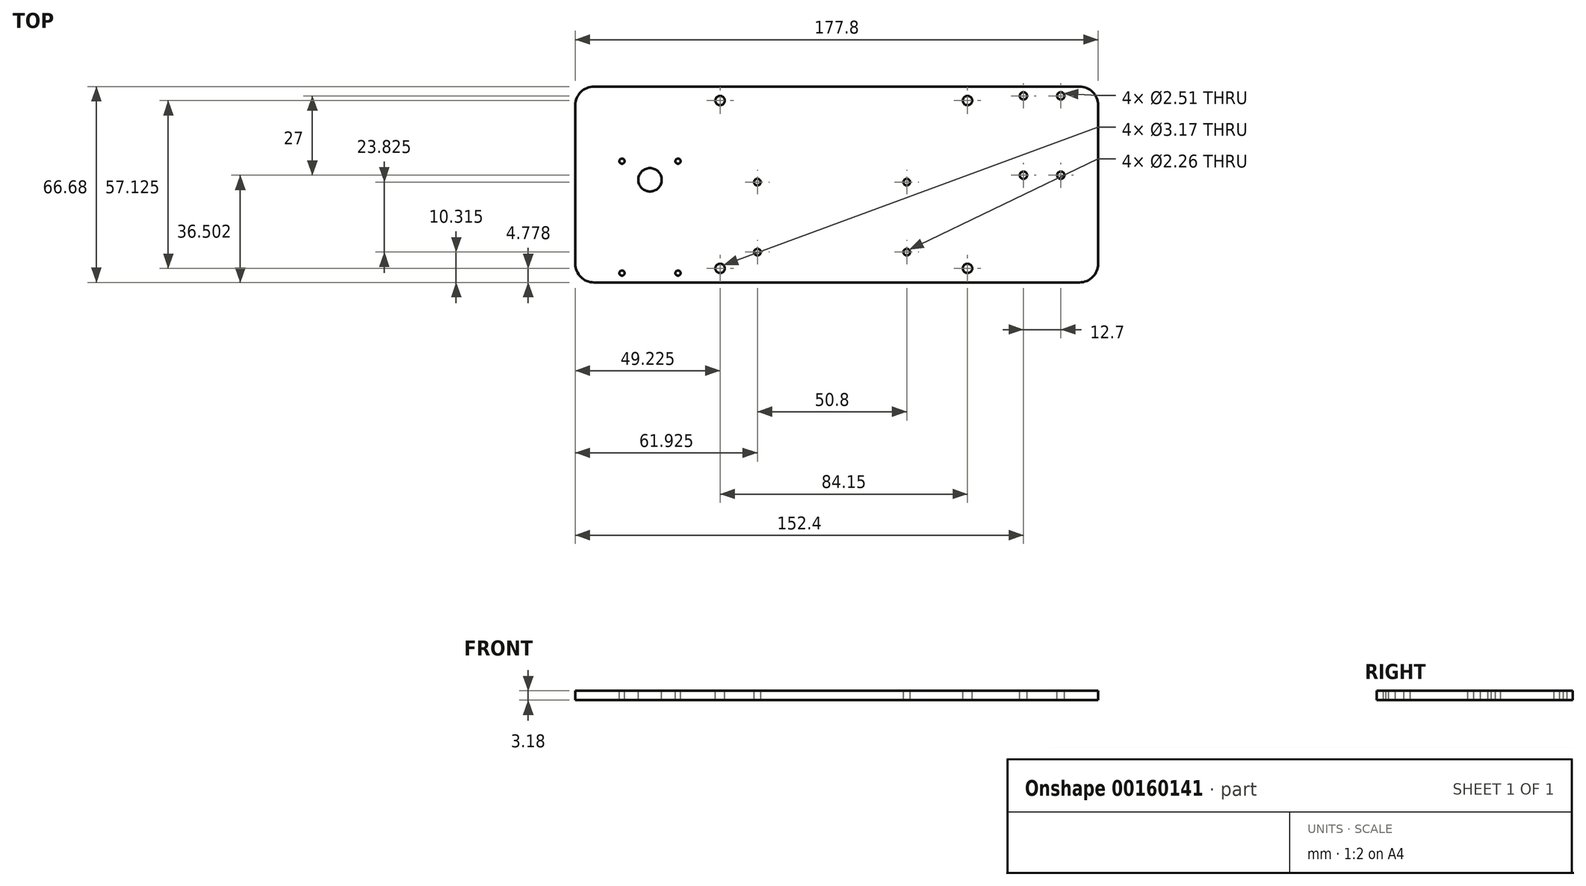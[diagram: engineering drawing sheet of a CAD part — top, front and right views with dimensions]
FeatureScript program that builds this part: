
annotation { "Feature Type Name" : "Feature", "Feature Type Description" : "" }
export const myFeature = defineFeature(function(context is Context, id is Id, definition is map)
    precondition{}
    {
        {
            var Q0;
            Q0=qCreatedBy(makeId("Top.planeOp"),FACE);
            var sketch = newSketch(context, id + "F0", { "sketchPlane" : qUnion([Q0])});
            skLineSegment(sketch, "E0.bottom", {"start": v(88.9, -33.34) * mm, "end": v(-88.9, -33.34) * mm});
            skLineSegment(sketch, "E0.top", {"start": v(88.9, 33.34) * mm, "end": v(-88.9, 33.34) * mm});
            skLineSegment(sketch, "E0.left", {"start": v(88.9, -33.34) * mm, "end": v(88.9, 33.34) * mm});
            skLineSegment(sketch, "E0.right", {"start": v(-88.9, -33.34) * mm, "end": v(-88.9, 33.34) * mm});
            skPoint(sketch, "E0.middle", {"position": v(0, 0) * mm});
            skSolve(sketch);
        }
        {
            var Q0;
            Q0 = qSketchRegion(id + "F0", true);
            extrude(context, id + "F1", {"entities" : qUnion([Q0]), "depth" : 3.17 * mm});
        }
        {
            var Q0;
            Q0=makeQuery(id+"F1.opExtrude","CAP_FACE",FACE,{"disambiguationData":[OSD([sQuery(id+"F0.wireOp",EDGE,"E0.bottom"),sQuery(id+"F0.wireOp",EDGE,"E0.top"),sQuery(id+"F0.wireOp",EDGE,"E0.left"),sQuery(id+"F0.wireOp",EDGE,"E0.right")])],"isStart":false});
            var sketch = newSketch(context, id + "F2", { "sketchPlane" : qUnion([Q0])});
            skLineSegment(sketch, "E1", {"start": v(-104.96, 26.99) * mm, "end": v(-63.7, 26.99) * mm, "construction": true});
            skLineSegment(sketch, "E2", {"start": v(-82.55, 35.77) * mm, "end": v(-82.55, 22.57) * mm, "construction": true});
            skArc(sketch, "E3", {"start": v(-82.55, 33.34) * mm, "mid": v(-87.04, 31.48) * mm, "end": v(-88.9, 26.99) * mm});
            skSolve(sketch);
        }
        {
            var Q0;
            Q0 = qSketchRegion(id + "F2", true);
            var Q1;
            {var subQ0=sQuery(id+"F2.wireOp",EDGE,"E3");Q1=makeQuery(id+"F2.imprint","IMPRINT",FACE,{"disambiguationData":[TD([[makeQuery(id+"F2.imprint","IMPRINT",EDGE,{"derivedFrom":subQ0}),-1.0]])]});}
            extrude(context, id + "F3", {"entities" : qUnion([Q0, Q1]), "operationType" : NewBodyOperationType.REMOVE, "endBound" : BoundingType.THROUGH_ALL, "oppositeDirection" : true, "depth" : 25.4 * mm});
        }
        {
            var Q0;
            Q0=makeQuery(id+"F1.opExtrude","CAP_FACE",FACE,{"disambiguationData":[OSD([sQuery(id+"F0.wireOp",EDGE,"E0.bottom"),sQuery(id+"F0.wireOp",EDGE,"E0.top"),sQuery(id+"F0.wireOp",EDGE,"E0.left"),sQuery(id+"F0.wireOp",EDGE,"E0.right")])],"isStart":false});
            var sketch = newSketch(context, id + "F4", { "sketchPlane" : qUnion([Q0])});
            skLineSegment(sketch, "E4", {"start": v(-93.93, -26.99) * mm, "end": v(97.13, -26.99) * mm, "construction": true});
            skLineSegment(sketch, "E5", {"start": v(-82.55, 36) * mm, "end": v(-82.55, -44.72) * mm, "construction": true});
            skLineSegment(sketch, "E6", {"start": v(82.55, 36.74) * mm, "end": v(82.55, -46.7) * mm, "construction": true});
            skLineSegment(sketch, "E7", {"start": v(-88.9, 26.99) * mm, "end": v(88.9, 26.99) * mm, "construction": true});
            skArc(sketch, "E8", {"start": v(-88.9, -26.99) * mm, "mid": v(-87.04, -31.48) * mm, "end": v(-82.55, -33.34) * mm});
            skArc(sketch, "E9", {"start": v(88.9, 26.99) * mm, "mid": v(87.04, 31.48) * mm, "end": v(82.55, 33.34) * mm});
            skArc(sketch, "E10", {"start": v(82.55, -33.34) * mm, "mid": v(87.04, -31.48) * mm, "end": v(88.9, -26.99) * mm});
            skSolve(sketch);
        }
        {
            var Q0;
            {var subQ0=sQuery(id+"F4.wireOp",EDGE,"E9");Q0=makeQuery(id+"F4.imprint","IMPRINT",FACE,{"disambiguationData":[TD([[makeQuery(id+"F4.imprint","IMPRINT",EDGE,{"derivedFrom":subQ0}),-1.0]])]});}
            var Q1;
            {var subQ0=sQuery(id+"F4.wireOp",EDGE,"E10");Q1=makeQuery(id+"F4.imprint","IMPRINT",FACE,{"disambiguationData":[TD([[makeQuery(id+"F4.imprint","IMPRINT",EDGE,{"derivedFrom":subQ0}),-1.0]])]});}
            var Q2;
            {var subQ0=sQuery(id+"F4.wireOp",EDGE,"E8");Q2=makeQuery(id+"F4.imprint","IMPRINT",FACE,{"disambiguationData":[TD([[makeQuery(id+"F4.imprint","IMPRINT",EDGE,{"derivedFrom":subQ0}),-1.0]])]});}
            extrude(context, id + "F5", {"entities" : qUnion([Q0, Q1, Q2]), "operationType" : NewBodyOperationType.REMOVE, "endBound" : BoundingType.THROUGH_ALL, "oppositeDirection" : true, "depth" : 25.4 * mm});
        }
        {
            var Q0;
            Q0=makeQuery(id+"F1.opExtrude","CAP_FACE",FACE,{"disambiguationData":[OSD([sQuery(id+"F0.wireOp",EDGE,"E0.bottom"),sQuery(id+"F0.wireOp",EDGE,"E0.top"),sQuery(id+"F0.wireOp",EDGE,"E0.left"),sQuery(id+"F0.wireOp",EDGE,"E0.right")])],"isStart":false});
            var sketch = newSketch(context, id + "F6", { "sketchPlane" : qUnion([Q0])});
            skLineSegment(sketch, "E11", {"start": v(-75.5, 30.16) * mm, "end": v(76.36, 30.16) * mm, "construction": true});
            skLineSegment(sketch, "E12", {"start": v(76.2, 36.57) * mm, "end": v(76.2, 3.16) * mm, "construction": true});
            skLineSegment(sketch, "E13", {"start": v(63.5, 36.77) * mm, "end": v(63.5, 3.16) * mm, "construction": true});
            skLineSegment(sketch, "E14", {"start": v(54.23, 3.16) * mm, "end": v(81, 3.16) * mm, "construction": true});
            skCircle(sketch, "E15", {"center": v(63.5, 30.16) * mm, "radius": 1.26 * mm});
            skCircle(sketch, "E16", {"center": v(76.2, 30.16) * mm, "radius": 1.26 * mm});
            skCircle(sketch, "E17", {"center": v(63.5, 3.16) * mm, "radius": 1.26 * mm});
            skCircle(sketch, "E18", {"center": v(76.2, 3.16) * mm, "radius": 1.26 * mm});
            skSolve(sketch);
        }
        {
            var Q0;
            Q0 = qSketchRegion(id + "F6", true);
            extrude(context, id + "F7", {"entities" : qUnion([Q0]), "operationType" : NewBodyOperationType.REMOVE, "endBound" : BoundingType.THROUGH_ALL, "oppositeDirection" : true, "depth" : 25.4 * mm});
        }
        {
            var Q0;
            Q0=makeQuery(id+"F1.opExtrude","CAP_FACE",FACE,{"disambiguationData":[OSD([sQuery(id+"F0.wireOp",EDGE,"E0.bottom"),sQuery(id+"F0.wireOp",EDGE,"E0.top"),sQuery(id+"F0.wireOp",EDGE,"E0.left"),sQuery(id+"F0.wireOp",EDGE,"E0.right")])],"isStart":false});
            var sketch = newSketch(context, id + "F8", { "sketchPlane" : qUnion([Q0])});
            skLineSegment(sketch, "E19", {"start": v(44.48, 28.56) * mm, "end": v(44.48, -28.56) * mm, "construction": true});
            skLineSegment(sketch, "E20", {"start": v(-39.67, 28.56) * mm, "end": v(-39.67, -28.56) * mm, "construction": true});
            skLineSegment(sketch, "E21", {"start": v(-39.67, -28.56) * mm, "end": v(44.48, -28.56) * mm, "construction": true});
            skLineSegment(sketch, "E22", {"start": v(-39.67, 28.56) * mm, "end": v(44.48, 28.56) * mm, "construction": true});
            skCircle(sketch, "E23", {"center": v(44.48, 28.56) * mm, "radius": 1.59 * mm});
            skCircle(sketch, "E24", {"center": v(-39.67, 28.56) * mm, "radius": 1.59 * mm});
            skCircle(sketch, "E25", {"center": v(-39.67, -28.56) * mm, "radius": 1.59 * mm});
            skCircle(sketch, "E26", {"center": v(44.48, -28.56) * mm, "radius": 1.59 * mm});
            skSolve(sketch);
        }
        {
            var Q0;
            Q0 = qSketchRegion(id + "F8", true);
            extrude(context, id + "F9", {"entities" : qUnion([Q0]), "operationType" : NewBodyOperationType.REMOVE, "endBound" : BoundingType.THROUGH_ALL, "oppositeDirection" : true, "depth" : 25.4 * mm});
        }
        {
            var Q0;
            Q0=makeQuery(id+"F1.opExtrude","CAP_FACE",FACE,{"disambiguationData":[OSD([sQuery(id+"F0.wireOp",EDGE,"E0.bottom"),sQuery(id+"F0.wireOp",EDGE,"E0.top"),sQuery(id+"F0.wireOp",EDGE,"E0.left"),sQuery(id+"F0.wireOp",EDGE,"E0.right")])],"isStart":false});
            var sketch = newSketch(context, id + "F10", { "sketchPlane" : qUnion([Q0])});
            skLineSegment(sketch, "E27", {"start": v(-76.57, 7.94) * mm, "end": v(-41.84, 7.94) * mm, "construction": true});
            skLineSegment(sketch, "E28", {"start": v(-74.45, -30.16) * mm, "end": v(-51.24, -30.16) * mm, "construction": true});
            skLineSegment(sketch, "E29", {"start": v(-73.03, 19.17) * mm, "end": v(-73.03, -53.87) * mm, "construction": true});
            skLineSegment(sketch, "E30", {"start": v(-53.98, 17.58) * mm, "end": v(-53.98, -54.33) * mm, "construction": true});
            skCircle(sketch, "E31", {"center": v(-73.03, 7.94) * mm, "radius": 0.89 * mm});
            skCircle(sketch, "E32", {"center": v(-53.98, 7.94) * mm, "radius": 0.89 * mm});
            skCircle(sketch, "E33", {"center": v(-73.03, -30.16) * mm, "radius": 0.89 * mm});
            skCircle(sketch, "E34", {"center": v(-53.98, -30.16) * mm, "radius": 0.89 * mm});
            skSolve(sketch);
        }
        {
            var Q0;
            Q0 = qSketchRegion(id + "F10", true);
            extrude(context, id + "F11", {"entities" : qUnion([Q0]), "operationType" : NewBodyOperationType.REMOVE, "endBound" : BoundingType.THROUGH_ALL, "oppositeDirection" : true, "depth" : 25.4 * mm});
        }
        {
            var Q0;
            Q0=makeQuery(id+"F1.opExtrude","CAP_FACE",FACE,{"disambiguationData":[OSD([sQuery(id+"F0.wireOp",EDGE,"E0.bottom"),sQuery(id+"F0.wireOp",EDGE,"E0.top"),sQuery(id+"F0.wireOp",EDGE,"E0.left"),sQuery(id+"F0.wireOp",EDGE,"E0.right")])],"isStart":false});
            var sketch = newSketch(context, id + "F12", { "sketchPlane" : qUnion([Q0])});
            skLineSegment(sketch, "E35", {"start": v(-99.2, 1.59) * mm, "end": v(-41.85, 1.59) * mm, "construction": true});
            skLineSegment(sketch, "E36", {"start": v(-63.5, 16.63) * mm, "end": v(-63.5, -36.81) * mm, "construction": true});
            skCircle(sketch, "E37", {"center": v(-63.5, 1.59) * mm, "radius": 3.98 * mm});
            skSolve(sketch);
        }
        {
            var Q0;
            Q0 = qSketchRegion(id + "F12", true);
            extrude(context, id + "F13", {"entities" : qUnion([Q0]), "operationType" : NewBodyOperationType.REMOVE, "endBound" : BoundingType.THROUGH_ALL, "oppositeDirection" : true, "depth" : 25.4 * mm});
        }
        {
            var Q0;
            Q0=makeQuery(id+"F1.opExtrude","CAP_FACE",FACE,{"disambiguationData":[OSD([sQuery(id+"F0.wireOp",EDGE,"E0.bottom"),sQuery(id+"F0.wireOp",EDGE,"E0.top"),sQuery(id+"F0.wireOp",EDGE,"E0.left"),sQuery(id+"F0.wireOp",EDGE,"E0.right")])],"isStart":false});
            var sketch = newSketch(context, id + "F14", { "sketchPlane" : qUnion([Q0])});
            skLineSegment(sketch, "E38", {"start": v(-33.95, -23.03) * mm, "end": v(44.85, -23.03) * mm, "construction": true});
            skLineSegment(sketch, "E39", {"start": v(-28.14, 0.8) * mm, "end": v(34.53, 0.8) * mm, "construction": true});
            skLineSegment(sketch, "E40", {"start": v(-26.97, 8) * mm, "end": v(-26.97, -25.96) * mm, "construction": true});
            skLineSegment(sketch, "E41", {"start": v(23.83, 9.29) * mm, "end": v(23.83, -25.96) * mm, "construction": true});
            skCircle(sketch, "E42", {"center": v(-26.97, 0.8) * mm, "radius": 1.13 * mm});
            skCircle(sketch, "E43", {"center": v(23.83, 0.8) * mm, "radius": 1.13 * mm});
            skCircle(sketch, "E44", {"center": v(23.83, -23.03) * mm, "radius": 1.13 * mm});
            skCircle(sketch, "E45", {"center": v(-26.97, -23.03) * mm, "radius": 1.13 * mm});
            skSolve(sketch);
        }
        {
            var Q0;
            Q0 = qSketchRegion(id + "F14", true);
            extrude(context, id + "F15", {"entities" : qUnion([Q0]), "operationType" : NewBodyOperationType.REMOVE, "endBound" : BoundingType.THROUGH_ALL, "oppositeDirection" : true, "depth" : 25.4 * mm});
        }
    });
